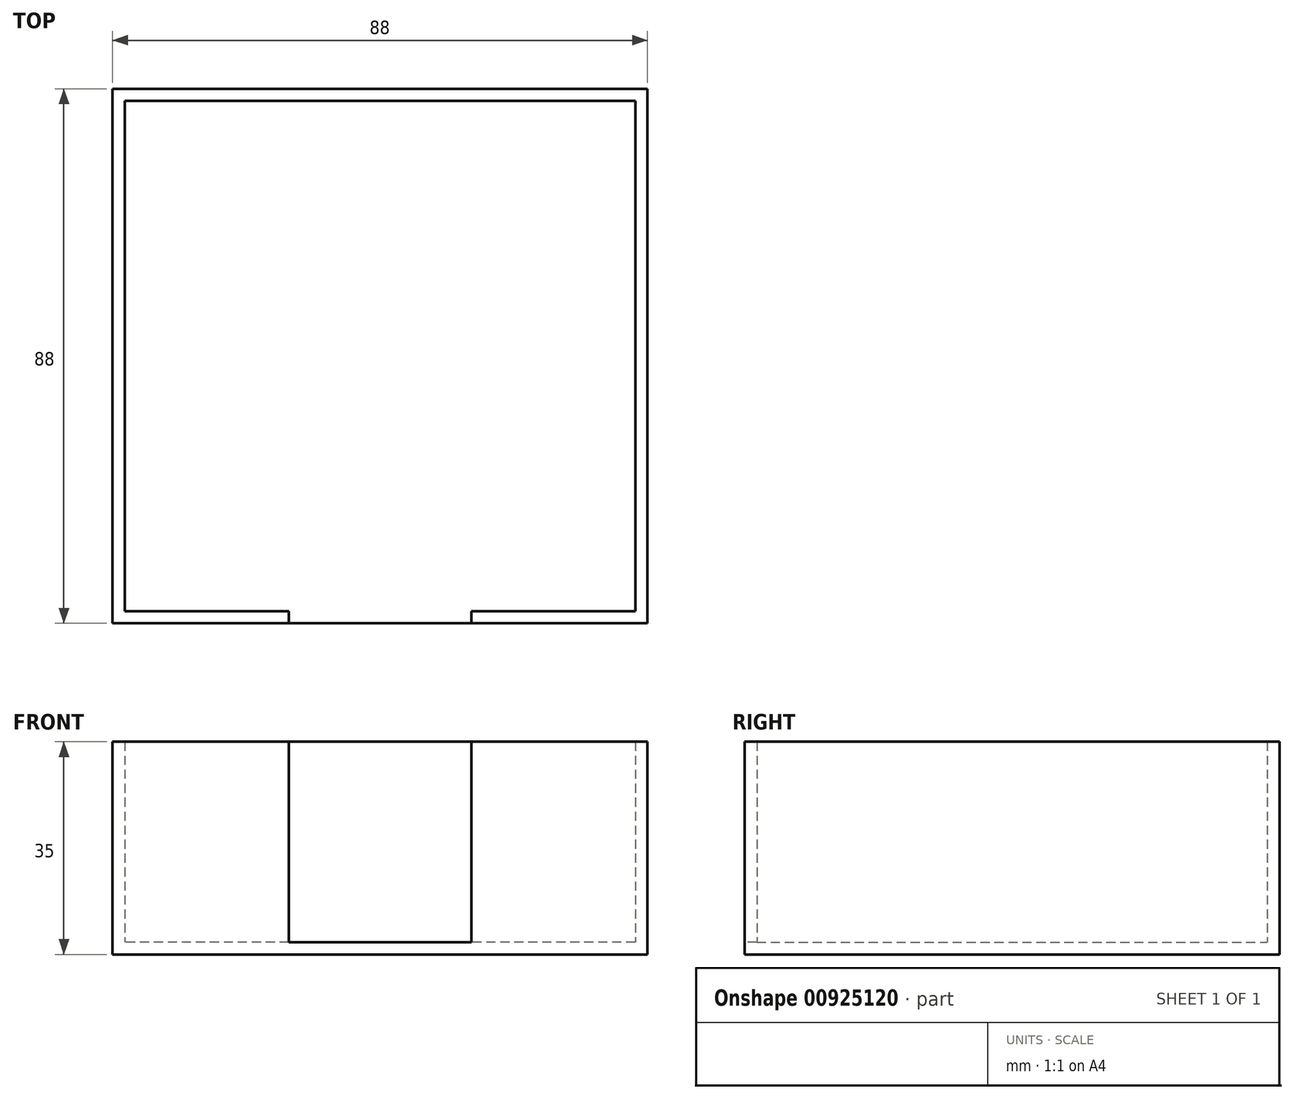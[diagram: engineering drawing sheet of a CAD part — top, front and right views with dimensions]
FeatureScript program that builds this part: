
annotation { "Feature Type Name" : "Feature", "Feature Type Description" : "" }
export const myFeature = defineFeature(function(context is Context, id is Id, definition is map)
    precondition{}
    {
        {
            var Q0;
            Q0=qCreatedBy(makeId("Top.planeOp"),FACE);
            var sketch = newSketch(context, id + "F0", { "sketchPlane" : qUnion([Q0])});
            skLineSegment(sketch, "E0.bottom", {"start": v(0, 0) * mm, "end": v(-88, 0) * mm});
            skLineSegment(sketch, "E0.top", {"start": v(0, 88) * mm, "end": v(-88, 88) * mm});
            skLineSegment(sketch, "E0.left", {"start": v(0, 0) * mm, "end": v(0, 88) * mm});
            skLineSegment(sketch, "E0.right", {"start": v(-88, 0) * mm, "end": v(-88, 88) * mm});
            skSolve(sketch);
        }
        {
            var Q0;
            Q0=makeQuery(id+"F0.imprint","IMPRINT",FACE,{"disambiguationData":[TD([[makeQuery(id+"F0.imprint","IMPRINT",EDGE,{"derivedFrom":sQuery(id+"F0.wireOp",EDGE,"E0.bottom")}),-1.0]])]});
            extrude(context, id + "F1", {"entities" : qUnion([Q0]), "depth" : 35 * mm, "offsetDistance" : 25 * mm});
        }
        {
            var Q0;
            Q0=makeQuery(id+"F1.opExtrude","CAP_FACE",FACE,{"disambiguationData":[OSD([sQuery(id+"F0.wireOp",EDGE,"E0.bottom"),sQuery(id+"F0.wireOp",EDGE,"E0.top"),sQuery(id+"F0.wireOp",EDGE,"E0.left"),sQuery(id+"F0.wireOp",EDGE,"E0.right")])],"isStart":false});
            shell(context, id + "F2", {"entities" : qUnion([Q0]), "thickness" : 2 * mm});
        }
        {
            var Q0;
            Q0=makeQuery(id+"F1.opExtrude","SWEPT_FACE",FACE,{"disambiguationData":[OSD([sQuery(id+"F0.wireOp",EDGE,"E0.bottom")])]});
            var sketch = newSketch(context, id + "F3", { "sketchPlane" : qUnion([Q0])});
            skLineSegment(sketch, "E1.bottom", {"start": v(-59, 35) * mm, "end": v(-29, 35) * mm});
            skLineSegment(sketch, "E1.top", {"start": v(-59, 2) * mm, "end": v(-29, 2) * mm});
            skLineSegment(sketch, "E1.left", {"start": v(-59, 35) * mm, "end": v(-59, 2) * mm});
            skLineSegment(sketch, "E1.right", {"start": v(-29, 35) * mm, "end": v(-29, 2) * mm});
            skLineSegment(sketch, "E2", {"start": v(-44, 35) * mm, "end": v(-44, 0) * mm, "construction": true});
            skSolve(sketch);
        }
        {
            var Q0;
            Q0 = qSketchRegion(id + "F3", true);
            extrude(context, id + "F4", {"entities" : qUnion([Q0]), "operationType" : NewBodyOperationType.REMOVE, "oppositeDirection" : true, "depth" : 25 * mm, "offsetDistance" : 25 * mm});
        }
    });
